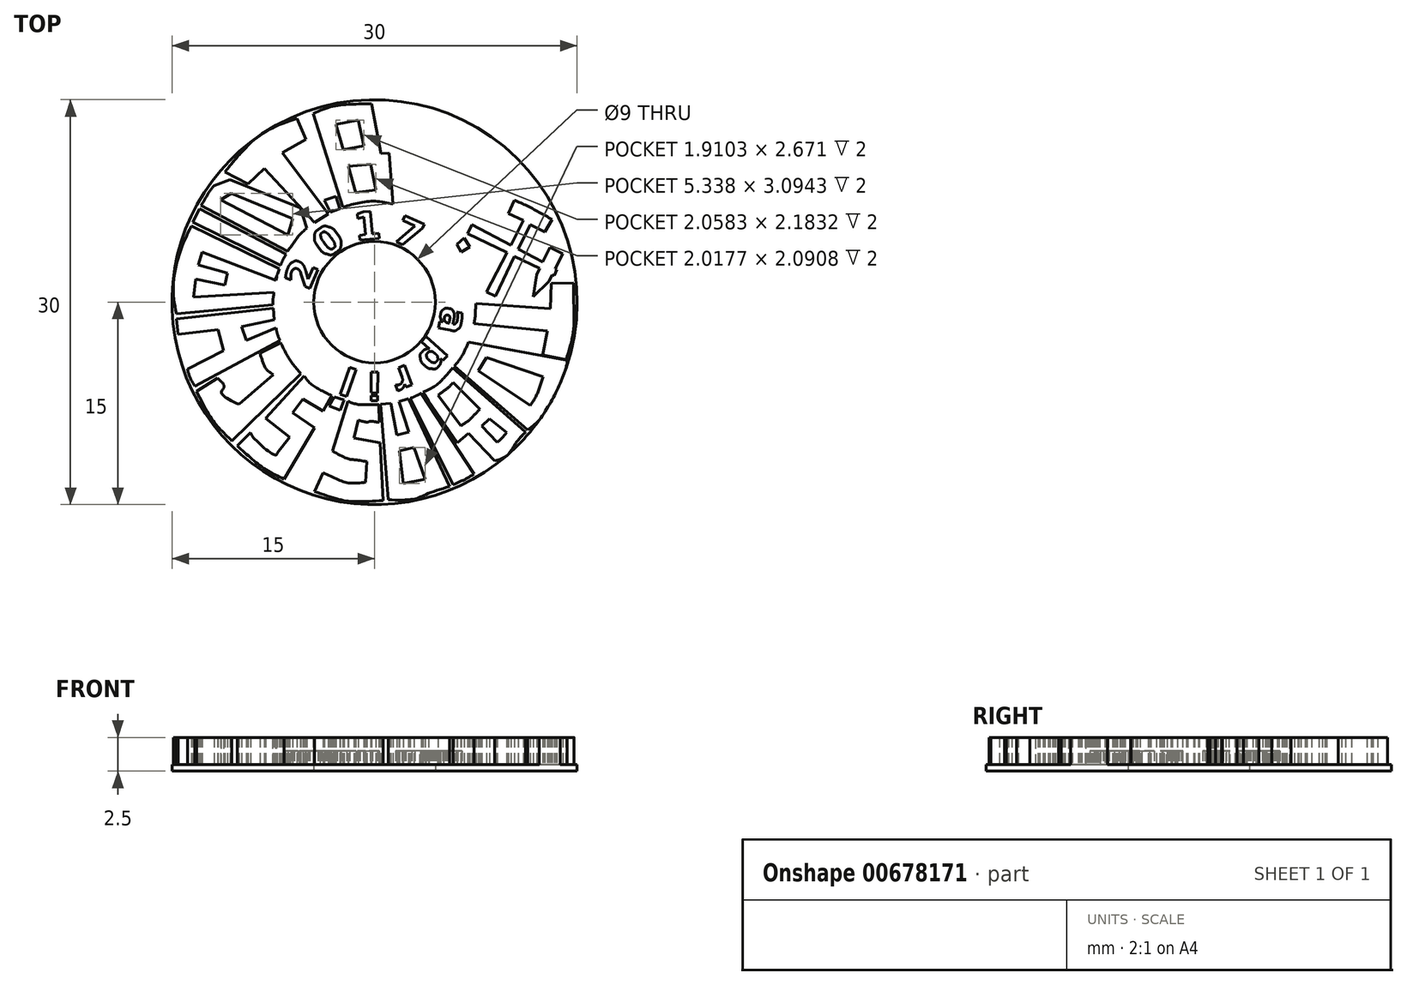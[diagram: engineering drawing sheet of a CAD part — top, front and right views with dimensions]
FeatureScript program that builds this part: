
annotation { "Feature Type Name" : "Feature", "Feature Type Description" : "" }
export const myFeature = defineFeature(function(context is Context, id is Id, definition is map)
    precondition{}
    {
        {
            var Q0;
            Q0=qCreatedBy(makeId("Top.planeOp"),FACE);
            var sketch = newSketch(context, id + "F0", { "sketchPlane" : qUnion([Q0])});
            skCircle(sketch, "E0", {"center": v(0, 0) * mm, "radius": 15 * mm});
            skCircle(sketch, "E1", {"center": v(0, 0) * mm, "radius": 4.5 * mm});
            skSolve(sketch);
        }
        {
            var Q0;
            Q0=makeQuery(id+"F0.imprint","IMPRINT",FACE,{"disambiguationData":[TD([[makeQuery(id+"F0.imprint","IMPRINT",EDGE,{"derivedFrom":sQuery(id+"F0.wireOp",EDGE,"E0")}),1.0]])]});
            extrude(context, id + "F1", {"entities" : qUnion([Q0]), "depth" : 0.5 * mm, "offsetDistance" : 25 * mm});
        }
        {
            var Q0;
            Q0=makeQuery(id+"F1.opExtrude","CAP_FACE",FACE,{"disambiguationData":[OSD([sQuery(id+"F0.wireOp",EDGE,"E0"),sQuery(id+"F0.wireOp",EDGE,"E1")])],"isStart":false});
            var sketch = newSketch(context, id + "F2", { "sketchPlane" : qUnion([Q0])});
            skFitSpline(sketch, "E2", {"points": [v(14.73, 1.43) * mm, v(14.75, -0.4) * mm, v(14.7, -2.22) * mm, v(14.19, -4.26) * mm]});
            skFitSpline(sketch, "E3", {"points": [v(7.35, -1.6) * mm, v(7.45, -1.1) * mm, v(7.47, -0.6) * mm, v(7.51, -0.08) * mm]});
            skLineSegment(sketch, "E4", {"start": v(14.19, -4.26) * mm, "end": v(12.44, -3.92) * mm});
            skLineSegment(sketch, "E5", {"start": v(12.44, -3.92) * mm, "end": v(12.8, -2.13) * mm});
            skLineSegment(sketch, "E6", {"start": v(12.8, -2.13) * mm, "end": v(7.35, -1.6) * mm});
            skLineSegment(sketch, "E7", {"start": v(7.51, -0.08) * mm, "end": v(13.02, -0.47) * mm});
            skLineSegment(sketch, "E8", {"start": v(13.02, -0.47) * mm, "end": v(13.07, 1.4) * mm});
            skLineSegment(sketch, "E9", {"start": v(13.07, 1.4) * mm, "end": v(14.73, 1.43) * mm});
            skFitSpline(sketch, "E10", {"points": [v(11.53, -7.64) * mm, v(11.97, -6.94) * mm, v(12.25, -6.24) * mm, v(12.47, -5.53) * mm]});
            skLineSegment(sketch, "E11", {"start": v(12.47, -5.53) * mm, "end": v(8.28, -4.1) * mm});
            skLineSegment(sketch, "E12", {"start": v(8.28, -4.1) * mm, "end": v(7.7, -5.08) * mm});
            skLineSegment(sketch, "E13", {"start": v(7.7, -5.08) * mm, "end": v(11.53, -7.64) * mm});
            skLineSegment(sketch, "E14", {"start": v(11.53, -7.64) * mm, "end": v(12.47, -5.53) * mm});
            skFitSpline(sketch, "E15", {"points": [v(5.91, -4.73) * mm, v(6.38, -4.14) * mm, v(6.7, -3.55) * mm, v(6.95, -2.96) * mm]});
            skLineSegment(sketch, "E16", {"start": v(11.34, -9.46) * mm, "end": v(5.91, -4.73) * mm});
            skLineSegment(sketch, "E17", {"start": v(5.91, -4.73) * mm, "end": v(11.34, -9.46) * mm});
            skFitSpline(sketch, "E18", {"points": [v(14.15, -4.3) * mm, v(14.25, -4.34) * mm, v(12.79, -7.94) * mm, v(11.34, -9.46) * mm]});
            skLineSegment(sketch, "E19", {"start": v(6.95, -2.96) * mm, "end": v(14.15, -4.3) * mm});
            skLineSegment(sketch, "E20", {"start": v(14.15, -4.3) * mm, "end": v(6.95, -2.96) * mm});
            skFitSpline(sketch, "E21", {"points": [v(9.07, -10.38) * mm, v(9.34, -10.18) * mm, v(9.55, -9.92) * mm, v(9.77, -9.67) * mm]});
            skLineSegment(sketch, "E22", {"start": v(7.95, -9.18) * mm, "end": v(9.07, -10.38) * mm});
            skLineSegment(sketch, "E23", {"start": v(9.07, -10.38) * mm, "end": v(7.95, -9.18) * mm});
            skLineSegment(sketch, "E24", {"start": v(9.77, -9.67) * mm, "end": v(8.52, -8.63) * mm});
            skLineSegment(sketch, "E25", {"start": v(8.52, -8.63) * mm, "end": v(7.95, -9.18) * mm});
            skFitSpline(sketch, "E26", {"points": [v(6.39, -9.15) * mm, v(6.92, -8.8) * mm, v(7.37, -8.37) * mm, v(7.8, -7.93) * mm]});
            skLineSegment(sketch, "E27", {"start": v(4.7, -6.9) * mm, "end": v(6.39, -9.15) * mm});
            skLineSegment(sketch, "E28", {"start": v(6.39, -9.15) * mm, "end": v(4.7, -6.9) * mm});
            skFitSpline(sketch, "E29", {"points": [v(5.82, -5.94) * mm, v(5.5, -6.3) * mm, v(5.1, -6.6) * mm, v(4.7, -6.9) * mm]});
            skLineSegment(sketch, "E30", {"start": v(7.8, -7.93) * mm, "end": v(5.82, -5.94) * mm});
            skLineSegment(sketch, "E31", {"start": v(5.82, -5.94) * mm, "end": v(7.8, -7.93) * mm});
            skFitSpline(sketch, "E32", {"points": [v(3.58, -6.68) * mm, v(4.51, -6.2) * mm, v(5.17, -5.57) * mm, v(5.8, -4.86) * mm]});
            skLineSegment(sketch, "E33", {"start": v(4, -7.35) * mm, "end": v(3.58, -6.68) * mm});
            skLineSegment(sketch, "E34", {"start": v(3.58, -6.68) * mm, "end": v(4, -7.35) * mm});
            skFitSpline(sketch, "E35", {"points": [v(11.17, -9.64) * mm, v(10.5, -10.38) * mm, v(9.8, -11.35) * mm, v(8.9, -11.76) * mm]});
            skLineSegment(sketch, "E36", {"start": v(5.8, -4.86) * mm, "end": v(11.17, -9.64) * mm});
            skLineSegment(sketch, "E37", {"start": v(11.17, -9.64) * mm, "end": v(5.8, -4.86) * mm});
            skFitSpline(sketch, "E38", {"points": [v(7.35, -12.74) * mm, v(6.84, -13.06) * mm, v(6.33, -13.3) * mm, v(5.82, -13.51) * mm]});
            skLineSegment(sketch, "E39", {"start": v(6.96, -9.71) * mm, "end": v(6.12, -10.4) * mm});
            skLineSegment(sketch, "E40", {"start": v(6.12, -10.4) * mm, "end": v(6.96, -9.71) * mm});
            skFitSpline(sketch, "E41", {"points": [v(2.65, -7.13) * mm, v(2.9, -7.02) * mm, v(3.15, -6.9) * mm, v(3.45, -6.75) * mm]});
            skLineSegment(sketch, "E42", {"start": v(5.82, -13.51) * mm, "end": v(2.65, -7.13) * mm});
            skLineSegment(sketch, "E43", {"start": v(2.65, -7.13) * mm, "end": v(5.82, -13.51) * mm});
            skLineSegment(sketch, "E44", {"start": v(3.45, -6.75) * mm, "end": v(7.35, -12.74) * mm});
            skLineSegment(sketch, "E45", {"start": v(7.35, -12.74) * mm, "end": v(3.45, -6.75) * mm});
            skFitSpline(sketch, "E46", {"points": [v(5.56, -13.64) * mm, v(3.67, -14.3) * mm, v(2.99, -14.58) * mm, v(1.01, -14.65) * mm]});
            skLineSegment(sketch, "E47", {"start": v(1.66, -9.85) * mm, "end": v(2.55, -9.63) * mm});
            skLineSegment(sketch, "E48", {"start": v(2.55, -9.63) * mm, "end": v(1.8, -7.38) * mm});
            skLineSegment(sketch, "E49", {"start": v(1.8, -7.38) * mm, "end": v(2.5, -7.14) * mm});
            skLineSegment(sketch, "E50", {"start": v(2.5, -7.14) * mm, "end": v(5.56, -13.64) * mm});
            skLineSegment(sketch, "E51", {"start": v(1.01, -14.65) * mm, "end": v(0.45, -7.57) * mm});
            skLineSegment(sketch, "E52", {"start": v(0.45, -7.57) * mm, "end": v(1.21, -7.5) * mm});
            skLineSegment(sketch, "E53", {"start": v(1.21, -7.5) * mm, "end": v(1.66, -9.85) * mm});
            skLineSegment(sketch, "E54", {"start": v(1.84, -11.03) * mm, "end": v(2.12, -13.45) * mm});
            skLineSegment(sketch, "E55", {"start": v(2.12, -13.45) * mm, "end": v(1.84, -11.03) * mm});
            skFitSpline(sketch, "E56", {"points": [v(-3.82, -12.64) * mm, v(-2.69, -13.16) * mm, v(-1.78, -13.4) * mm, v(-0.65, -13.34) * mm]});
            skLineSegment(sketch, "E57", {"start": v(3.75, -13.1) * mm, "end": v(2.9, -10.78) * mm});
            skLineSegment(sketch, "E58", {"start": v(2.9, -10.78) * mm, "end": v(1.84, -11.03) * mm});
            skFitSpline(sketch, "E59", {"points": [v(-0.58, -11.82) * mm, v(-1.52, -11.67) * mm, v(-1.91, -11.62) * mm, v(-3.13, -11.03) * mm]});
            skLineSegment(sketch, "E60", {"start": v(-0.65, -13.34) * mm, "end": v(-0.58, -11.82) * mm});
            skLineSegment(sketch, "E61", {"start": v(-0.58, -11.82) * mm, "end": v(-0.65, -13.34) * mm});
            skFitSpline(sketch, "E62", {"points": [v(-1.96, -7.34) * mm, v(-1.27, -7.57) * mm, v(-0.48, -7.6) * mm, v(0.31, -7.6) * mm]});
            skLineSegment(sketch, "E63", {"start": v(-3.13, -11.03) * mm, "end": v(-1.96, -7.34) * mm});
            skLineSegment(sketch, "E64", {"start": v(-1.96, -7.34) * mm, "end": v(-3.13, -11.03) * mm});
            skFitSpline(sketch, "E65", {"points": [v(0.36, -8.9) * mm, v(-0.37, -8.84) * mm, v(-0.5, -8.88) * mm, v(-1.2, -8.75) * mm]});
            skLineSegment(sketch, "E66", {"start": v(0.31, -7.6) * mm, "end": v(0.36, -8.9) * mm});
            skLineSegment(sketch, "E67", {"start": v(0.36, -8.9) * mm, "end": v(0.31, -7.6) * mm});
            skFitSpline(sketch, "E68", {"points": [v(0.63, -14.69) * mm, v(-1.45, -14.77) * mm, v(-2.66, -14.61) * mm, v(-4.45, -14.02) * mm]});
            skLineSegment(sketch, "E69", {"start": v(-1.2, -8.75) * mm, "end": v(-1.54, -10.08) * mm});
            skLineSegment(sketch, "E70", {"start": v(-1.54, -10.08) * mm, "end": v(0.43, -10.4) * mm});
            skLineSegment(sketch, "E71", {"start": v(0.43, -10.4) * mm, "end": v(0.63, -14.69) * mm});
            skLineSegment(sketch, "E72", {"start": v(-4.45, -14.02) * mm, "end": v(-3.82, -12.64) * mm});
            skLineSegment(sketch, "E73", {"start": v(-3.82, -12.64) * mm, "end": v(-4.45, -14.02) * mm});
            skFitSpline(sketch, "E74", {"points": [v(-9.19, -9.65) * mm, v(-8.9, -10.1) * mm, v(-7.32, -11.34) * mm, v(-7.2, -11.17) * mm]});
            skLineSegment(sketch, "E75", {"start": v(-2.54, -8) * mm, "end": v(-3.35, -7.68) * mm});
            skLineSegment(sketch, "E76", {"start": v(-3.35, -7.68) * mm, "end": v(-2.98, -7.03) * mm});
            skLineSegment(sketch, "E77", {"start": v(-2.98, -7.03) * mm, "end": v(-2.27, -7.26) * mm});
            skLineSegment(sketch, "E78", {"start": v(-2.27, -7.26) * mm, "end": v(-2.54, -8) * mm});
            skFitSpline(sketch, "E79", {"points": [v(-5.21, -5.46) * mm, v(-4.86, -5.92) * mm, v(-4.15, -6.42) * mm, v(-3.16, -6.93) * mm]});
            skLineSegment(sketch, "E80", {"start": v(-7.2, -11.17) * mm, "end": v(-6.28, -9.99) * mm});
            skLineSegment(sketch, "E81", {"start": v(-6.28, -9.99) * mm, "end": v(-7.2, -11.17) * mm});
            skFitSpline(sketch, "E82", {"points": [v(-6.7, -13.1) * mm, v(-8, -12.43) * mm, v(-9.12, -11.58) * mm, v(-10.16, -10.64) * mm]});
            skLineSegment(sketch, "E83", {"start": v(-3.16, -6.93) * mm, "end": v(-3.8, -8.06) * mm});
            skLineSegment(sketch, "E84", {"start": v(-3.8, -8.06) * mm, "end": v(-5.29, -7.16) * mm});
            skLineSegment(sketch, "E85", {"start": v(-5.29, -7.16) * mm, "end": v(-6.05, -8.18) * mm});
            skLineSegment(sketch, "E86", {"start": v(-6.05, -8.18) * mm, "end": v(-4.45, -9.3) * mm});
            skLineSegment(sketch, "E87", {"start": v(-4.45, -9.3) * mm, "end": v(-6.7, -13.1) * mm});
            skFitSpline(sketch, "E88", {"points": [v(-6.95, -3) * mm, v(-6.51, -3.87) * mm, v(-6.05, -4.59) * mm, v(-5.45, -5.3) * mm]});
            skLineSegment(sketch, "E89", {"start": v(-10.16, -10.64) * mm, "end": v(-9.19, -9.65) * mm});
            skLineSegment(sketch, "E90", {"start": v(-9.19, -9.65) * mm, "end": v(-10.16, -10.64) * mm});
            skFitSpline(sketch, "E91", {"points": [v(-10.56, -10.28) * mm, v(-11.34, -9.5) * mm, v(-12.13, -8.55) * mm, v(-13.18, -6.6) * mm]});
            skLineSegment(sketch, "E92", {"start": v(-5.45, -5.3) * mm, "end": v(-10.56, -10.28) * mm});
            skLineSegment(sketch, "E93", {"start": v(-10.56, -10.28) * mm, "end": v(-5.45, -5.3) * mm});
            skFitSpline(sketch, "E94", {"points": [v(-11.62, -5.63) * mm, v(-11.14, -6.26) * mm, v(-11.33, -6.7) * mm, v(-10.05, -7.57) * mm]});
            skLineSegment(sketch, "E95", {"start": v(-13.18, -6.6) * mm, "end": v(-11.62, -5.63) * mm});
            skLineSegment(sketch, "E96", {"start": v(-11.62, -5.63) * mm, "end": v(-13.18, -6.6) * mm});
            skFitSpline(sketch, "E97", {"points": [v(-7.49, -5.38) * mm, v(-8.05, -4.92) * mm, v(-8.3, -4.36) * mm, v(-8.48, -3.8) * mm]});
            skLineSegment(sketch, "E98", {"start": v(-10.05, -7.57) * mm, "end": v(-7.49, -5.38) * mm});
            skLineSegment(sketch, "E99", {"start": v(-7.49, -5.38) * mm, "end": v(-10.05, -7.57) * mm});
            skFitSpline(sketch, "E100", {"points": [v(-13.32, -6.22) * mm, v(-13.55, -5.82) * mm, v(-13.73, -5.4) * mm, v(-13.85, -4.96) * mm]});
            skLineSegment(sketch, "E101", {"start": v(-8.48, -3.8) * mm, "end": v(-6.95, -3) * mm});
            skLineSegment(sketch, "E102", {"start": v(-6.95, -3) * mm, "end": v(-8.48, -3.8) * mm});
            skFitSpline(sketch, "E103", {"points": [v(-7.3, -1.92) * mm, v(-7.22, -2.26) * mm, v(-7.12, -2.56) * mm, v(-7, -2.84) * mm]});
            skLineSegment(sketch, "E104", {"start": v(-13.85, -4.96) * mm, "end": v(-11.17, -3.6) * mm});
            skLineSegment(sketch, "E105", {"start": v(-11.17, -3.6) * mm, "end": v(-11.6, -2.05) * mm});
            skLineSegment(sketch, "E106", {"start": v(-11.6, -2.05) * mm, "end": v(-14.54, -2.4) * mm});
            skLineSegment(sketch, "E107", {"start": v(-14.54, -2.4) * mm, "end": v(-14.67, -1.23) * mm});
            skLineSegment(sketch, "E108", {"start": v(-14.67, -1.23) * mm, "end": v(-7.5, -0.45) * mm});
            skLineSegment(sketch, "E109", {"start": v(-7.5, -0.45) * mm, "end": v(-7.42, -1.31) * mm});
            skLineSegment(sketch, "E110", {"start": v(-7.42, -1.31) * mm, "end": v(-9.83, -1.81) * mm});
            skLineSegment(sketch, "E111", {"start": v(-9.83, -1.81) * mm, "end": v(-9.5, -2.83) * mm});
            skLineSegment(sketch, "E112", {"start": v(-9.5, -2.83) * mm, "end": v(-7.3, -1.92) * mm});
            skFitSpline(sketch, "E113", {"points": [v(-14.68, -0.86) * mm, v(-14.9, 1.2) * mm, v(-14.4, 3.7) * mm, v(-13.56, 5.66) * mm]});
            skLineSegment(sketch, "E114", {"start": v(-7, -2.84) * mm, "end": v(-13.32, -6.22) * mm});
            skLineSegment(sketch, "E115", {"start": v(-13.32, -6.22) * mm, "end": v(-7, -2.84) * mm});
            skFitSpline(sketch, "E116", {"points": [v(-7.04, 2.48) * mm, v(-7.3, 1.75) * mm, v(-7.24, 1.88) * mm, v(-7.3, 1.6) * mm]});
            skLineSegment(sketch, "E117", {"start": v(-13.56, 5.66) * mm, "end": v(-7.04, 2.48) * mm});
            skLineSegment(sketch, "E118", {"start": v(-7.04, 2.48) * mm, "end": v(-13.56, 5.66) * mm});
            skFitSpline(sketch, "E119", {"points": [v(-7.45, 0.73) * mm, v(-7.5, 0.36) * mm, v(-7.53, 0.17) * mm, v(-7.52, -0.2) * mm]});
            skLineSegment(sketch, "E120", {"start": v(-7.3, 1.6) * mm, "end": v(-12.78, 3.7) * mm});
            skLineSegment(sketch, "E121", {"start": v(-12.78, 3.7) * mm, "end": v(-13.06, 2.74) * mm});
            skLineSegment(sketch, "E122", {"start": v(-13.06, 2.74) * mm, "end": v(-10.9, 2.16) * mm});
            skLineSegment(sketch, "E123", {"start": v(-10.9, 2.16) * mm, "end": v(-11.08, 1.28) * mm});
            skLineSegment(sketch, "E124", {"start": v(-11.08, 1.28) * mm, "end": v(-13.25, 1.7) * mm});
            skLineSegment(sketch, "E125", {"start": v(-13.25, 1.7) * mm, "end": v(-13.4, 0.36) * mm});
            skLineSegment(sketch, "E126", {"start": v(-13.4, 0.36) * mm, "end": v(-7.45, 0.73) * mm});
            skLineSegment(sketch, "E127", {"start": v(-7.52, -0.2) * mm, "end": v(-14.68, -0.86) * mm});
            skLineSegment(sketch, "E128", {"start": v(-14.68, -0.86) * mm, "end": v(-7.52, -0.2) * mm});
            skFitSpline(sketch, "E129", {"points": [v(-6.55, 3.54) * mm, v(-6.71, 3.27) * mm, v(-6.85, 3) * mm, v(-6.96, 2.73) * mm]});
            skLineSegment(sketch, "E130", {"start": v(-13.47, 5.94) * mm, "end": v(-12.97, 6.91) * mm});
            skLineSegment(sketch, "E131", {"start": v(-12.97, 6.91) * mm, "end": v(-6.55, 3.54) * mm});
            skLineSegment(sketch, "E132", {"start": v(-6.96, 2.73) * mm, "end": v(-13.47, 5.94) * mm});
            skLineSegment(sketch, "E133", {"start": v(-13.47, 5.94) * mm, "end": v(-6.96, 2.73) * mm});
            skLineSegment(sketch, "E134", {"start": v(-11.41, 7.57) * mm, "end": v(-6.42, 4.98) * mm});
            skLineSegment(sketch, "E135", {"start": v(-6.42, 4.98) * mm, "end": v(-6.07, 6.2) * mm});
            skLineSegment(sketch, "E136", {"start": v(-6.07, 6.2) * mm, "end": v(-10.6, 8.08) * mm});
            skLineSegment(sketch, "E137", {"start": v(-10.6, 8.08) * mm, "end": v(-11.41, 7.57) * mm});
            skFitSpline(sketch, "E138", {"points": [v(-5, 5.48) * mm, v(-5.61, 4.92) * mm, v(-6.05, 4.3) * mm, v(-6.45, 3.78) * mm]});
            skLineSegment(sketch, "E139", {"start": v(-11.88, 8.63) * mm, "end": v(-10.7, 9.08) * mm});
            skLineSegment(sketch, "E140", {"start": v(-10.7, 9.08) * mm, "end": v(-5.49, 6.98) * mm});
            skLineSegment(sketch, "E141", {"start": v(-5.49, 6.98) * mm, "end": v(-5, 5.48) * mm});
            skFitSpline(sketch, "E142", {"points": [v(-12.85, 7.16) * mm, v(-12.55, 7.64) * mm, v(-12.28, 8.1) * mm, v(-11.88, 8.63) * mm]});
            skLineSegment(sketch, "E143", {"start": v(-6.45, 3.78) * mm, "end": v(-12.85, 7.16) * mm});
            skLineSegment(sketch, "E144", {"start": v(-12.85, 7.16) * mm, "end": v(-6.45, 3.78) * mm});
            skFitSpline(sketch, "E145", {"points": [v(-11.09, 9.64) * mm, v(-9.23, 11.74) * mm, v(-7.65, 12.86) * mm, v(-5.74, 13.62) * mm]});
            skLineSegment(sketch, "E146", {"start": v(-5.74, 13.62) * mm, "end": v(-5.1, 12.06) * mm});
            skLineSegment(sketch, "E147", {"start": v(-5.1, 12.06) * mm, "end": v(-6.83, 11.07) * mm});
            skLineSegment(sketch, "E148", {"start": v(-6.83, 11.07) * mm, "end": v(-3.44, 6.55) * mm});
            skLineSegment(sketch, "E149", {"start": v(-3.44, 6.55) * mm, "end": v(-4.46, 5.9) * mm});
            skLineSegment(sketch, "E150", {"start": v(-4.46, 5.9) * mm, "end": v(-8.17, 9.89) * mm});
            skLineSegment(sketch, "E151", {"start": v(-8.17, 9.89) * mm, "end": v(-9.35, 8.76) * mm});
            skLineSegment(sketch, "E152", {"start": v(-9.35, 8.76) * mm, "end": v(-11.09, 9.64) * mm});
            skLineSegment(sketch, "E153", {"start": v(-3.71, 7.54) * mm, "end": v(-2.87, 7.83) * mm});
            skLineSegment(sketch, "E154", {"start": v(-2.87, 7.83) * mm, "end": v(-2.58, 6.92) * mm});
            skLineSegment(sketch, "E155", {"start": v(-2.58, 6.92) * mm, "end": v(-3.26, 6.67) * mm});
            skLineSegment(sketch, "E156", {"start": v(-3.26, 6.67) * mm, "end": v(-3.71, 7.54) * mm});
            skLineSegment(sketch, "E157", {"start": v(-1.21, 13.5) * mm, "end": v(-2.84, 13.18) * mm});
            skLineSegment(sketch, "E158", {"start": v(-2.84, 13.18) * mm, "end": v(-2.31, 11.31) * mm});
            skLineSegment(sketch, "E159", {"start": v(-2.31, 11.31) * mm, "end": v(-0.78, 11.6) * mm});
            skLineSegment(sketch, "E160", {"start": v(-0.78, 11.6) * mm, "end": v(-1.21, 13.5) * mm});
            skFitSpline(sketch, "E161", {"points": [v(1.37, 7.27) * mm, v(0.13, 7.47) * mm, v(-1.11, 7.37) * mm, v(-2.35, 7.04) * mm]});
            skLineSegment(sketch, "E162", {"start": v(0.1, 8.3) * mm, "end": v(-0.28, 10.22) * mm});
            skLineSegment(sketch, "E163", {"start": v(-0.28, 10.22) * mm, "end": v(-1.93, 10.06) * mm});
            skLineSegment(sketch, "E164", {"start": v(-1.93, 10.06) * mm, "end": v(-1.4, 8.13) * mm});
            skLineSegment(sketch, "E165", {"start": v(-1.4, 8.13) * mm, "end": v(0.1, 8.3) * mm});
            skFitSpline(sketch, "E166", {"points": [v(-4.54, 13.98) * mm, v(-3.1, 14.5) * mm, v(-1.66, 14.66) * mm, v(-0.22, 14.71) * mm]});
            skLineSegment(sketch, "E167", {"start": v(-2.35, 7.04) * mm, "end": v(-4.54, 13.98) * mm});
            skLineSegment(sketch, "E168", {"start": v(-4.54, 13.98) * mm, "end": v(-2.35, 7.04) * mm});
            skLineSegment(sketch, "E169", {"start": v(-0.22, 14.71) * mm, "end": v(0.5, 11.02) * mm});
            skLineSegment(sketch, "E170", {"start": v(0.5, 11.02) * mm, "end": v(-0.22, 14.71) * mm});
            skLineSegment(sketch, "E171", {"start": v(1.08, 11.05) * mm, "end": v(1.37, 7.27) * mm});
            skLineSegment(sketch, "E172", {"start": v(1.37, 7.27) * mm, "end": v(1.08, 11.05) * mm});
            skLineSegment(sketch, "E173", {"start": v(5.12, 12.03) * mm, "end": v(2.66, 12.72) * mm});
            skLineSegment(sketch, "E174", {"start": v(2.66, 12.72) * mm, "end": v(5.12, 12.03) * mm});
            skFitSpline(sketch, "E175", {"points": [v(4.36, 6) * mm, v(3.46, 6.62) * mm, v(1.52, 7.3) * mm, v(1.5, 7.23) * mm]});
            skLineSegment(sketch, "E176", {"start": v(2.62, 11.45) * mm, "end": v(4.8, 10.63) * mm});
            skLineSegment(sketch, "E177", {"start": v(4.8, 10.63) * mm, "end": v(4.36, 6) * mm});
            skFitSpline(sketch, "E178", {"points": [v(1.3, 14.64) * mm, v(2.74, 14.5) * mm, v(4.13, 14.23) * mm, v(5.35, 13.67) * mm]});
            skLineSegment(sketch, "E179", {"start": v(1.5, 7.23) * mm, "end": v(1.55, 8.78) * mm});
            skLineSegment(sketch, "E180", {"start": v(1.55, 8.78) * mm, "end": v(3.73, 7.9) * mm});
            skLineSegment(sketch, "E181", {"start": v(3.73, 7.9) * mm, "end": v(3.8, 9.25) * mm});
            skLineSegment(sketch, "E182", {"start": v(3.8, 9.25) * mm, "end": v(1.5, 10.2) * mm});
            skLineSegment(sketch, "E183", {"start": v(1.5, 10.2) * mm, "end": v(1.3, 14.64) * mm});
            skLineSegment(sketch, "E184", {"start": v(5.35, 13.67) * mm, "end": v(5.12, 12.03) * mm});
            skLineSegment(sketch, "E185", {"start": v(5.12, 12.03) * mm, "end": v(5.35, 13.67) * mm});
            skLineSegment(sketch, "E186", {"start": v(8.2, 8.17) * mm, "end": v(7.57, 6.97) * mm});
            skLineSegment(sketch, "E187", {"start": v(7.57, 6.97) * mm, "end": v(8.2, 8.17) * mm});
            skFitSpline(sketch, "E188", {"points": [v(5.97, 4.44) * mm, v(5.57, 4.9) * mm, v(5.23, 5.26) * mm, v(4.56, 5.82) * mm]});
            skLineSegment(sketch, "E189", {"start": v(6.2, 8.12) * mm, "end": v(5.73, 6.4) * mm});
            skLineSegment(sketch, "E190", {"start": v(5.73, 6.4) * mm, "end": v(6.73, 5.34) * mm});
            skLineSegment(sketch, "E191", {"start": v(6.73, 5.34) * mm, "end": v(5.97, 4.44) * mm});
            skLineSegment(sketch, "E192", {"start": v(4.56, 5.82) * mm, "end": v(5.43, 10.26) * mm});
            skLineSegment(sketch, "E193", {"start": v(5.43, 10.26) * mm, "end": v(8.2, 8.17) * mm});
            skLineSegment(sketch, "E194", {"start": v(6.63, 4.74) * mm, "end": v(7.05, 4.1) * mm});
            skLineSegment(sketch, "E195", {"start": v(7.05, 4.1) * mm, "end": v(6.42, 3.72) * mm});
            skLineSegment(sketch, "E196", {"start": v(6.42, 3.72) * mm, "end": v(6.09, 4.28) * mm});
            skLineSegment(sketch, "E197", {"start": v(6.09, 4.28) * mm, "end": v(6.63, 4.74) * mm});
            skFitSpline(sketch, "E198", {"points": [v(10.34, 7.56) * mm, v(11.24, 7.16) * mm, v(12.2, 6.65) * mm, v(13.15, 6.13) * mm]});
            skLineSegment(sketch, "E199", {"start": v(13.15, 2.04) * mm, "end": v(12.92, 1.57) * mm});
            skLineSegment(sketch, "E200", {"start": v(12.92, 1.57) * mm, "end": v(11.75, 0.4) * mm});
            skLineSegment(sketch, "E201", {"start": v(11.75, 0.4) * mm, "end": v(11.99, 2.04) * mm});
            skLineSegment(sketch, "E202", {"start": v(11.99, 2.04) * mm, "end": v(12.22, 2.5) * mm});
            skLineSegment(sketch, "E203", {"start": v(12.22, 2.5) * mm, "end": v(10.36, 3.4) * mm});
            skLineSegment(sketch, "E204", {"start": v(10.36, 3.4) * mm, "end": v(8.94, 0.43) * mm});
            skLineSegment(sketch, "E205", {"start": v(8.94, 0.43) * mm, "end": v(8.28, 0.77) * mm});
            skLineSegment(sketch, "E206", {"start": v(8.28, 0.77) * mm, "end": v(9.8, 3.67) * mm});
            skLineSegment(sketch, "E207", {"start": v(9.8, 3.67) * mm, "end": v(6.89, 5.09) * mm});
            skLineSegment(sketch, "E208", {"start": v(6.89, 5.09) * mm, "end": v(7.22, 5.76) * mm});
            skLineSegment(sketch, "E209", {"start": v(7.22, 5.76) * mm, "end": v(10.1, 4.23) * mm});
            skLineSegment(sketch, "E210", {"start": v(10.1, 4.23) * mm, "end": v(11.02, 6.06) * mm});
            skLineSegment(sketch, "E211", {"start": v(11.02, 6.06) * mm, "end": v(9.92, 6.56) * mm});
            skLineSegment(sketch, "E212", {"start": v(9.92, 6.56) * mm, "end": v(10.34, 7.56) * mm});
            skFitSpline(sketch, "E213", {"points": [v(5.56, -1.3) * mm, v(5.58, -1.2) * mm, v(5.58, -1.12) * mm, v(5.55, -1.06) * mm]});
            skFitSpline(sketch, "E214", {"points": [v(5.55, -1.06) * mm, v(5.53, -1) * mm, v(5.48, -0.97) * mm, v(5.42, -0.96) * mm]});
            skFitSpline(sketch, "E215", {"points": [v(5.42, -0.96) * mm, v(5.35, -0.95) * mm, v(5.3, -0.96) * mm, v(5.26, -1) * mm]});
            skFitSpline(sketch, "E216", {"points": [v(5.26, -1) * mm, v(5.22, -1.03) * mm, v(5.19, -1.08) * mm, v(5.17, -1.15) * mm]});
            skFitSpline(sketch, "E217", {"points": [v(5.17, -1.15) * mm, v(5.16, -1.24) * mm, v(5.17, -1.33) * mm, v(5.23, -1.4) * mm]});
            skFitSpline(sketch, "E218", {"points": [v(5.23, -1.4) * mm, v(5.28, -1.48) * mm, v(5.36, -1.52) * mm, v(5.45, -1.54) * mm]});
            skLineSegment(sketch, "E219", {"start": v(13.15, 6.13) * mm, "end": v(12.6, 5.2) * mm});
            skLineSegment(sketch, "E220", {"start": v(12.6, 5.2) * mm, "end": v(11.53, 5.75) * mm});
            skLineSegment(sketch, "E221", {"start": v(11.53, 5.75) * mm, "end": v(10.63, 3.94) * mm});
            skLineSegment(sketch, "E222", {"start": v(10.63, 3.94) * mm, "end": v(12.46, 2.97) * mm});
            skLineSegment(sketch, "E223", {"start": v(12.46, 2.97) * mm, "end": v(13, 4.05) * mm});
            skLineSegment(sketch, "E224", {"start": v(13, 4.05) * mm, "end": v(13.92, 3.58) * mm});
            skLineSegment(sketch, "E225", {"start": v(13.92, 3.58) * mm, "end": v(13.38, 2.48) * mm});
            skLineSegment(sketch, "E226", {"start": v(13.38, 2.48) * mm, "end": v(13.5, 2.41) * mm});
            skLineSegment(sketch, "E227", {"start": v(13.5, 2.41) * mm, "end": v(13.29, 1.98) * mm});
            skLineSegment(sketch, "E228", {"start": v(13.29, 1.98) * mm, "end": v(13.15, 2.04) * mm});
            skLineSegment(sketch, "E229", {"start": v(5.45, -1.54) * mm, "end": v(5.51, -1.55) * mm});
            skLineSegment(sketch, "E230", {"start": v(5.51, -1.55) * mm, "end": v(5.56, -1.3) * mm});
            skLineSegment(sketch, "E231", {"start": v(5.56, -1.3) * mm, "end": v(5.56, -1.3) * mm});
            skFitSpline(sketch, "E232", {"points": [v(5.05, -1.47) * mm, v(4.97, -1.38) * mm, v(4.92, -1.3) * mm, v(4.9, -1.2) * mm]});
            skFitSpline(sketch, "E233", {"points": [v(4.9, -1.2) * mm, v(4.87, -1.12) * mm, v(4.87, -1.02) * mm, v(4.89, -0.9) * mm]});
            skFitSpline(sketch, "E234", {"points": [v(4.89, -0.9) * mm, v(4.92, -0.74) * mm, v(5, -0.62) * mm, v(5.1, -0.54) * mm]});
            skFitSpline(sketch, "E235", {"points": [v(5.1, -0.54) * mm, v(5.21, -0.46) * mm, v(5.34, -0.44) * mm, v(5.49, -0.47) * mm]});
            skFitSpline(sketch, "E236", {"points": [v(5.49, -0.47) * mm, v(5.66, -0.5) * mm, v(5.78, -0.59) * mm, v(5.84, -0.73) * mm]});
            skFitSpline(sketch, "E237", {"points": [v(5.84, -0.73) * mm, v(5.9, -0.86) * mm, v(5.9, -1.06) * mm, v(5.85, -1.33) * mm]});
            skLineSegment(sketch, "E238", {"start": v(5.6, -2.08) * mm, "end": v(4.73, -1.91) * mm});
            skLineSegment(sketch, "E239", {"start": v(4.73, -1.91) * mm, "end": v(4.83, -1.42) * mm});
            skLineSegment(sketch, "E240", {"start": v(4.83, -1.42) * mm, "end": v(5.05, -1.47) * mm});
            skFitSpline(sketch, "E241", {"points": [v(5.84, -1.62) * mm, v(5.91, -1.63) * mm, v(5.97, -1.61) * mm, v(6.02, -1.56) * mm]});
            skFitSpline(sketch, "E242", {"points": [v(6.02, -1.56) * mm, v(6.07, -1.5) * mm, v(6.1, -1.42) * mm, v(6.13, -1.29) * mm]});
            skFitSpline(sketch, "E243", {"points": [v(6.13, -1.29) * mm, v(6.15, -1.18) * mm, v(6.16, -1.09) * mm, v(6.16, -1) * mm]});
            skFitSpline(sketch, "E244", {"points": [v(6.16, -1) * mm, v(6.15, -0.9) * mm, v(6.14, -0.81) * mm, v(6.11, -0.73) * mm]});
            skLineSegment(sketch, "E245", {"start": v(5.85, -1.33) * mm, "end": v(5.8, -1.61) * mm});
            skLineSegment(sketch, "E246", {"start": v(5.8, -1.61) * mm, "end": v(5.84, -1.62) * mm});
            skFitSpline(sketch, "E247", {"points": [v(6.48, -0.8) * mm, v(6.49, -0.9) * mm, v(6.48, -1.01) * mm, v(6.48, -1.12) * mm]});
            skFitSpline(sketch, "E248", {"points": [v(6.48, -1.12) * mm, v(6.47, -1.23) * mm, v(6.46, -1.33) * mm, v(6.44, -1.44) * mm]});
            skFitSpline(sketch, "E249", {"points": [v(6.44, -1.44) * mm, v(6.38, -1.71) * mm, v(6.29, -1.9) * mm, v(6.16, -2) * mm]});
            skFitSpline(sketch, "E250", {"points": [v(6.16, -2) * mm, v(6.03, -2.1) * mm, v(5.84, -2.13) * mm, v(5.6, -2.08) * mm]});
            skLineSegment(sketch, "E251", {"start": v(6.11, -0.73) * mm, "end": v(6.48, -0.8) * mm});
            skLineSegment(sketch, "E252", {"start": v(6.48, -0.8) * mm, "end": v(6.11, -0.73) * mm});
            skLineSegment(sketch, "E253", {"start": v(5.6, -2.08) * mm, "end": v(5.6, -2.08) * mm});
            skFitSpline(sketch, "E254", {"points": [v(4.9, -4.18) * mm, v(4.92, -4.3) * mm, v(4.92, -4.4) * mm, v(4.9, -4.48) * mm]});
            skFitSpline(sketch, "E255", {"points": [v(4.9, -4.48) * mm, v(4.87, -4.57) * mm, v(4.82, -4.66) * mm, v(4.75, -4.74) * mm]});
            skFitSpline(sketch, "E256", {"points": [v(4.75, -4.74) * mm, v(4.63, -4.88) * mm, v(4.47, -4.95) * mm, v(4.27, -4.94) * mm]});
            skFitSpline(sketch, "E257", {"points": [v(4.27, -4.94) * mm, v(4.08, -4.93) * mm, v(3.9, -4.85) * mm, v(3.71, -4.69) * mm]});
            skFitSpline(sketch, "E258", {"points": [v(3.71, -4.69) * mm, v(3.54, -4.53) * mm, v(3.43, -4.35) * mm, v(3.4, -4.16) * mm]});
            skFitSpline(sketch, "E259", {"points": [v(3.4, -4.16) * mm, v(3.37, -3.97) * mm, v(3.41, -3.8) * mm, v(3.54, -3.66) * mm]});
            skFitSpline(sketch, "E260", {"points": [v(3.54, -3.66) * mm, v(3.61, -3.58) * mm, v(3.7, -3.52) * mm, v(3.78, -3.5) * mm]});
            skFitSpline(sketch, "E261", {"points": [v(3.78, -3.5) * mm, v(3.86, -3.46) * mm, v(3.96, -3.45) * mm, v(4.08, -3.45) * mm]});
            skLineSegment(sketch, "E262", {"start": v(4.08, -3.45) * mm, "end": v(3.47, -2.92) * mm});
            skLineSegment(sketch, "E263", {"start": v(3.47, -2.92) * mm, "end": v(3.8, -2.55) * mm});
            skLineSegment(sketch, "E264", {"start": v(3.8, -2.55) * mm, "end": v(5.4, -3.96) * mm});
            skLineSegment(sketch, "E265", {"start": v(5.4, -3.96) * mm, "end": v(5.06, -4.33) * mm});
            skLineSegment(sketch, "E266", {"start": v(5.06, -4.33) * mm, "end": v(4.9, -4.18) * mm});
            skFitSpline(sketch, "E267", {"points": [v(4.6, -4.36) * mm, v(4.68, -4.28) * mm, v(4.7, -4.2) * mm, v(4.68, -4.1) * mm]});
            skFitSpline(sketch, "E268", {"points": [v(4.68, -4.1) * mm, v(4.66, -4.01) * mm, v(4.6, -3.91) * mm, v(4.49, -3.82) * mm]});
            skFitSpline(sketch, "E269", {"points": [v(4.49, -3.82) * mm, v(4.38, -3.72) * mm, v(4.27, -3.67) * mm, v(4.18, -3.66) * mm]});
            skFitSpline(sketch, "E270", {"points": [v(4.18, -3.66) * mm, v(4.08, -3.65) * mm, v(4, -3.68) * mm, v(3.93, -3.76) * mm]});
            skFitSpline(sketch, "E271", {"points": [v(3.93, -3.76) * mm, v(3.86, -3.84) * mm, v(3.83, -3.93) * mm, v(3.86, -4.02) * mm]});
            skFitSpline(sketch, "E272", {"points": [v(3.86, -4.02) * mm, v(3.88, -4.11) * mm, v(3.94, -4.2) * mm, v(4.05, -4.3) * mm]});
            skFitSpline(sketch, "E273", {"points": [v(4.05, -4.3) * mm, v(4.16, -4.4) * mm, v(4.26, -4.46) * mm, v(4.36, -4.47) * mm]});
            skFitSpline(sketch, "E274", {"points": [v(4.36, -4.47) * mm, v(4.45, -4.48) * mm, v(4.54, -4.44) * mm, v(4.6, -4.36) * mm]});
            skLineSegment(sketch, "E275", {"start": v(4.08, -3.45) * mm, "end": v(4.08, -3.45) * mm});
            skFitSpline(sketch, "E276", {"points": [v(1.56, -6.15) * mm, v(1.6, -6.15) * mm, v(1.65, -6.15) * mm, v(1.7, -6.14) * mm]});
            skFitSpline(sketch, "E277", {"points": [v(1.7, -6.14) * mm, v(1.74, -6.13) * mm, v(1.78, -6.12) * mm, v(1.82, -6.1) * mm]});
            skFitSpline(sketch, "E278", {"points": [v(1.82, -6.1) * mm, v(1.94, -6.06) * mm, v(2.01, -5.99) * mm, v(2.05, -5.89) * mm]});
            skFitSpline(sketch, "E279", {"points": [v(2.05, -5.89) * mm, v(2.08, -5.79) * mm, v(2.07, -5.67) * mm, v(2.02, -5.53) * mm]});
            skFitSpline(sketch, "E280", {"points": [v(2.23, -6.07) * mm, v(2.2, -6.18) * mm, v(2.16, -6.28) * mm, v(2.1, -6.35) * mm]});
            skFitSpline(sketch, "E281", {"points": [v(2.1, -6.35) * mm, v(2.04, -6.42) * mm, v(1.96, -6.48) * mm, v(1.85, -6.52) * mm]});
            skFitSpline(sketch, "E282", {"points": [v(1.85, -6.52) * mm, v(1.83, -6.53) * mm, v(1.82, -6.53) * mm, v(1.8, -6.54) * mm]});
            skFitSpline(sketch, "E283", {"points": [v(1.8, -6.54) * mm, v(1.78, -6.55) * mm, v(1.75, -6.55) * mm, v(1.72, -6.56) * mm]});
            skLineSegment(sketch, "E284", {"start": v(2.02, -5.53) * mm, "end": v(1.76, -4.86) * mm});
            skLineSegment(sketch, "E285", {"start": v(1.76, -4.86) * mm, "end": v(2.23, -4.69) * mm});
            skLineSegment(sketch, "E286", {"start": v(2.23, -4.69) * mm, "end": v(2.78, -6.13) * mm});
            skLineSegment(sketch, "E287", {"start": v(2.78, -6.13) * mm, "end": v(2.32, -6.3) * mm});
            skLineSegment(sketch, "E288", {"start": v(2.32, -6.3) * mm, "end": v(2.23, -6.07) * mm});
            skLineSegment(sketch, "E289", {"start": v(1.72, -6.56) * mm, "end": v(1.56, -6.15) * mm});
            skLineSegment(sketch, "E290", {"start": v(1.56, -6.15) * mm, "end": v(1.56, -6.15) * mm});
            skLineSegment(sketch, "E291", {"start": v(1.56, -6.15) * mm, "end": v(1.72, -6.56) * mm});
            skLineSegment(sketch, "E292", {"start": v(0.23, -6.72) * mm, "end": v(-0.26, -6.72) * mm});
            skLineSegment(sketch, "E293", {"start": v(-0.26, -6.72) * mm, "end": v(-0.25, -5.17) * mm});
            skLineSegment(sketch, "E294", {"start": v(-0.25, -5.17) * mm, "end": v(0.24, -5.18) * mm});
            skLineSegment(sketch, "E295", {"start": v(0.24, -5.18) * mm, "end": v(0.23, -6.72) * mm});
            skLineSegment(sketch, "E296", {"start": v(0.23, -6.72) * mm, "end": v(0.23, -6.72) * mm});
            skLineSegment(sketch, "E297", {"start": v(0.23, -7.32) * mm, "end": v(-0.27, -7.32) * mm});
            skLineSegment(sketch, "E298", {"start": v(-0.27, -7.32) * mm, "end": v(-0.26, -6.91) * mm});
            skLineSegment(sketch, "E299", {"start": v(-0.26, -6.91) * mm, "end": v(0.23, -6.92) * mm});
            skLineSegment(sketch, "E300", {"start": v(0.23, -6.92) * mm, "end": v(0.23, -7.32) * mm});
            skLineSegment(sketch, "E301", {"start": v(0.23, -7.32) * mm, "end": v(0.23, -7.32) * mm});
            skLineSegment(sketch, "E302", {"start": v(-2.08, -7) * mm, "end": v(-2.55, -6.84) * mm});
            skLineSegment(sketch, "E303", {"start": v(-2.55, -6.84) * mm, "end": v(-1.83, -4.81) * mm});
            skLineSegment(sketch, "E304", {"start": v(-1.83, -4.81) * mm, "end": v(-1.37, -4.98) * mm});
            skLineSegment(sketch, "E305", {"start": v(-1.37, -4.98) * mm, "end": v(-2.08, -7) * mm});
            skFitSpline(sketch, "E306", {"points": [v(-5.45, 2.14) * mm, v(-5.48, 2.22) * mm, v(-5.51, 2.3) * mm, v(-5.55, 2.34) * mm]});
            skFitSpline(sketch, "E307", {"points": [v(-5.55, 2.34) * mm, v(-5.6, 2.4) * mm, v(-5.64, 2.44) * mm, v(-5.7, 2.46) * mm]});
            skFitSpline(sketch, "E308", {"points": [v(-5.7, 2.46) * mm, v(-5.79, 2.5) * mm, v(-5.87, 2.5) * mm, v(-5.95, 2.46) * mm]});
            skFitSpline(sketch, "E309", {"points": [v(-5.95, 2.46) * mm, v(-6.03, 2.43) * mm, v(-6.1, 2.36) * mm, v(-6.14, 2.26) * mm]});
            skFitSpline(sketch, "E310", {"points": [v(-6.14, 2.26) * mm, v(-6.17, 2.19) * mm, v(-6.19, 2.1) * mm, v(-6.2, 2) * mm]});
            skFitSpline(sketch, "E311", {"points": [v(-6.2, 2) * mm, v(-6.2, 1.89) * mm, v(-6.2, 1.77) * mm, v(-6.18, 1.64) * mm]});
            skLineSegment(sketch, "E312", {"start": v(-4.9, 1.72) * mm, "end": v(-4.54, 2.55) * mm});
            skLineSegment(sketch, "E313", {"start": v(-4.54, 2.55) * mm, "end": v(-4.19, 2.4) * mm});
            skLineSegment(sketch, "E314", {"start": v(-4.19, 2.4) * mm, "end": v(-4.78, 1.03) * mm});
            skLineSegment(sketch, "E315", {"start": v(-4.78, 1.03) * mm, "end": v(-5.14, 1.18) * mm});
            skLineSegment(sketch, "E316", {"start": v(-5.14, 1.18) * mm, "end": v(-5.45, 2.14) * mm});
            skFitSpline(sketch, "E317", {"points": [v(-6.6, 1.82) * mm, v(-6.58, 1.95) * mm, v(-6.56, 2.07) * mm, v(-6.53, 2.18) * mm]});
            skFitSpline(sketch, "E318", {"points": [v(-6.53, 2.18) * mm, v(-6.5, 2.3) * mm, v(-6.47, 2.4) * mm, v(-6.42, 2.5) * mm]});
            skFitSpline(sketch, "E319", {"points": [v(-6.42, 2.5) * mm, v(-6.33, 2.74) * mm, v(-6.2, 2.89) * mm, v(-6.05, 2.97) * mm]});
            skFitSpline(sketch, "E320", {"points": [v(-6.05, 2.97) * mm, v(-5.9, 3.05) * mm, v(-5.73, 3.05) * mm, v(-5.55, 2.98) * mm]});
            skFitSpline(sketch, "E321", {"points": [v(-5.55, 2.98) * mm, v(-5.44, 2.93) * mm, v(-5.36, 2.86) * mm, v(-5.3, 2.77) * mm]});
            skFitSpline(sketch, "E322", {"points": [v(-5.3, 2.77) * mm, v(-5.23, 2.68) * mm, v(-5.16, 2.52) * mm, v(-5.08, 2.28) * mm]});
            skLineSegment(sketch, "E323", {"start": v(-6.18, 1.64) * mm, "end": v(-6.6, 1.82) * mm});
            skLineSegment(sketch, "E324", {"start": v(-6.6, 1.82) * mm, "end": v(-6.18, 1.64) * mm});
            skFitSpline(sketch, "E325", {"points": [v(-3.2, 4.76) * mm, v(-3.36, 4.97) * mm, v(-3.49, 5.1) * mm, v(-3.59, 5.16) * mm]});
            skFitSpline(sketch, "E326", {"points": [v(-3.59, 5.16) * mm, v(-3.69, 5.21) * mm, v(-3.78, 5.2) * mm, v(-3.88, 5.14) * mm]});
            skFitSpline(sketch, "E327", {"points": [v(-3.88, 5.14) * mm, v(-3.97, 5.08) * mm, v(-4, 4.98) * mm, v(-3.98, 4.87) * mm]});
            skFitSpline(sketch, "E328", {"points": [v(-3.98, 4.87) * mm, v(-3.96, 4.76) * mm, v(-3.87, 4.6) * mm, v(-3.72, 4.39) * mm]});
            skFitSpline(sketch, "E329", {"points": [v(-3.72, 4.39) * mm, v(-3.57, 4.18) * mm, v(-3.44, 4.04) * mm, v(-3.34, 3.99) * mm]});
            skFitSpline(sketch, "E330", {"points": [v(-3.34, 3.99) * mm, v(-3.24, 3.93) * mm, v(-3.14, 3.93) * mm, v(-3.05, 4) * mm]});
            skFitSpline(sketch, "E331", {"points": [v(-3.05, 4) * mm, v(-2.96, 4.07) * mm, v(-2.92, 4.16) * mm, v(-2.94, 4.27) * mm]});
            skFitSpline(sketch, "E332", {"points": [v(-2.94, 4.27) * mm, v(-2.97, 4.39) * mm, v(-3.06, 4.55) * mm, v(-3.2, 4.76) * mm]});
            skLineSegment(sketch, "E333", {"start": v(-5.08, 2.28) * mm, "end": v(-4.9, 1.72) * mm});
            skLineSegment(sketch, "E334", {"start": v(-4.9, 1.72) * mm, "end": v(-5.08, 2.28) * mm});
            skFitSpline(sketch, "E335", {"points": [v(-2.78, 5.07) * mm, v(-2.58, 4.8) * mm, v(-2.48, 4.54) * mm, v(-2.5, 4.3) * mm]});
            skFitSpline(sketch, "E336", {"points": [v(-2.5, 4.3) * mm, v(-2.5, 4.07) * mm, v(-2.62, 3.87) * mm, v(-2.83, 3.7) * mm]});
            skFitSpline(sketch, "E337", {"points": [v(-2.83, 3.7) * mm, v(-3.05, 3.55) * mm, v(-3.28, 3.5) * mm, v(-3.5, 3.56) * mm]});
            skFitSpline(sketch, "E338", {"points": [v(-3.5, 3.56) * mm, v(-3.73, 3.63) * mm, v(-3.95, 3.8) * mm, v(-4.15, 4.07) * mm]});
            skFitSpline(sketch, "E339", {"points": [v(-4.15, 4.07) * mm, v(-4.35, 4.35) * mm, v(-4.44, 4.6) * mm, v(-4.43, 4.84) * mm]});
            skFitSpline(sketch, "E340", {"points": [v(-4.43, 4.84) * mm, v(-4.42, 5.08) * mm, v(-4.3, 5.28) * mm, v(-4.09, 5.44) * mm]});
            skFitSpline(sketch, "E341", {"points": [v(-4.09, 5.44) * mm, v(-3.87, 5.6) * mm, v(-3.65, 5.64) * mm, v(-3.42, 5.58) * mm]});
            skFitSpline(sketch, "E342", {"points": [v(-3.42, 5.58) * mm, v(-3.2, 5.52) * mm, v(-2.98, 5.35) * mm, v(-2.78, 5.07) * mm]});
            skLineSegment(sketch, "E343", {"start": v(-1.12, 4.96) * mm, "end": v(-0.65, 5) * mm});
            skLineSegment(sketch, "E344", {"start": v(-0.65, 5) * mm, "end": v(-0.78, 6.33) * mm});
            skLineSegment(sketch, "E345", {"start": v(-0.78, 6.33) * mm, "end": v(-1.25, 6.18) * mm});
            skLineSegment(sketch, "E346", {"start": v(-1.25, 6.18) * mm, "end": v(-1.29, 6.54) * mm});
            skLineSegment(sketch, "E347", {"start": v(-1.29, 6.54) * mm, "end": v(-0.82, 6.69) * mm});
            skLineSegment(sketch, "E348", {"start": v(-0.82, 6.69) * mm, "end": v(-0.32, 6.74) * mm});
            skLineSegment(sketch, "E349", {"start": v(-0.32, 6.74) * mm, "end": v(-0.16, 5.05) * mm});
            skLineSegment(sketch, "E350", {"start": v(-0.16, 5.05) * mm, "end": v(0.31, 5.1) * mm});
            skLineSegment(sketch, "E351", {"start": v(0.31, 5.1) * mm, "end": v(0.35, 4.73) * mm});
            skLineSegment(sketch, "E352", {"start": v(0.35, 4.73) * mm, "end": v(-1.09, 4.6) * mm});
            skLineSegment(sketch, "E353", {"start": v(-1.09, 4.6) * mm, "end": v(-1.12, 4.96) * mm});
            skLineSegment(sketch, "E354", {"start": v(2.26, 6.42) * mm, "end": v(3.67, 5.77) * mm});
            skLineSegment(sketch, "E355", {"start": v(3.67, 5.77) * mm, "end": v(3.54, 5.5) * mm});
            skLineSegment(sketch, "E356", {"start": v(3.54, 5.5) * mm, "end": v(2.07, 4.24) * mm});
            skLineSegment(sketch, "E357", {"start": v(2.07, 4.24) * mm, "end": v(1.6, 4.46) * mm});
            skLineSegment(sketch, "E358", {"start": v(1.6, 4.46) * mm, "end": v(3, 5.65) * mm});
            skLineSegment(sketch, "E359", {"start": v(3, 5.65) * mm, "end": v(2.1, 6.07) * mm});
            skLineSegment(sketch, "E360", {"start": v(2.1, 6.07) * mm, "end": v(2.26, 6.42) * mm});
            skLineSegment(sketch, "E361", {"start": v(0.5, 11.02) * mm, "end": v(1.08, 11.05) * mm});
            skLineSegment(sketch, "E362", {"start": v(2.62, 11.45) * mm, "end": v(2.66, 12.72) * mm});
            skLineSegment(sketch, "E363", {"start": v(6.2, 8.12) * mm, "end": v(7.57, 6.97) * mm});
            skLineSegment(sketch, "E364", {"start": v(6.96, -9.71) * mm, "end": v(8.9, -11.76) * mm});
            skLineSegment(sketch, "E365", {"start": v(4, -7.35) * mm, "end": v(6.12, -10.4) * mm});
            skLineSegment(sketch, "E366", {"start": v(2.12, -13.45) * mm, "end": v(3.75, -13.1) * mm});
            skLineSegment(sketch, "E367", {"start": v(-8.06, -8.62) * mm, "end": v(-6.28, -9.99) * mm});
            skLineSegment(sketch, "E368", {"start": v(-8.06, -8.62) * mm, "end": v(-5.21, -5.46) * mm});
            skSolve(sketch);
        }
        {
            var Q0;
            Q0=makeQuery(id+"F2.imprint","IMPRINT",FACE,{"disambiguationData":[TD([[makeQuery(id+"F2.imprint","IMPRINT",EDGE,{"derivedFrom":sQuery(id+"F2.wireOp",EDGE,"E74")}),-1.0]])]});
            var Q1;
            Q1=makeQuery(id+"F2.imprint","IMPRINT",FACE,{"disambiguationData":[TD([[makeQuery(id+"F2.imprint","IMPRINT",EDGE,{"derivedFrom":sQuery(id+"F2.wireOp",EDGE,"E88")}),-1.0]])]});
            var Q2;
            Q2=makeQuery(id+"F2.imprint","IMPRINT",FACE,{"disambiguationData":[TD([[makeQuery(id+"F2.imprint","IMPRINT",EDGE,{"derivedFrom":sQuery(id+"F2.wireOp",EDGE,"E100")}),-1.0]])]});
            var Q3;
            Q3=makeQuery(id+"F2.imprint","IMPRINT",FACE,{"disambiguationData":[TD([[makeQuery(id+"F2.imprint","IMPRINT",EDGE,{"derivedFrom":sQuery(id+"F2.wireOp",EDGE,"E113")}),-1.0]])]});
            var Q4;
            Q4=makeQuery(id+"F2.imprint","IMPRINT",FACE,{"disambiguationData":[TD([[makeQuery(id+"F2.imprint","IMPRINT",EDGE,{"derivedFrom":sQuery(id+"F2.wireOp",EDGE,"E129")}),-1.0]])]});
            var Q5;
            Q5=makeQuery(id+"F2.imprint","IMPRINT",FACE,{"disambiguationData":[TD([[makeQuery(id+"F2.imprint","IMPRINT",EDGE,{"derivedFrom":sQuery(id+"F2.wireOp",EDGE,"E134")}),-1.0]])]});
            var Q6;
            Q6=makeQuery(id+"F2.imprint","IMPRINT",FACE,{"disambiguationData":[TD([[makeQuery(id+"F2.imprint","IMPRINT",EDGE,{"derivedFrom":sQuery(id+"F2.wireOp",EDGE,"E145")}),-1.0]])]});
            var Q7;
            Q7=makeQuery(id+"F2.imprint","IMPRINT",FACE,{"disambiguationData":[TD([[makeQuery(id+"F2.imprint","IMPRINT",EDGE,{"derivedFrom":sQuery(id+"F2.wireOp",EDGE,"E153")}),-1.0]])]});
            var Q8;
            Q8=makeQuery(id+"F2.imprint","IMPRINT",FACE,{"disambiguationData":[TD([[makeQuery(id+"F2.imprint","IMPRINT",EDGE,{"derivedFrom":sQuery(id+"F2.wireOp",EDGE,"E157")}),-1.0]])]});
            var Q9;
            Q9=makeQuery(id+"F2.imprint","IMPRINT",FACE,{"disambiguationData":[TD([[makeQuery(id+"F2.imprint","IMPRINT",EDGE,{"derivedFrom":sQuery(id+"F2.wireOp",EDGE,"E174")}),1.0]])]});
            var Q10;
            Q10=makeQuery(id+"F2.imprint","IMPRINT",FACE,{"disambiguationData":[TD([[makeQuery(id+"F2.imprint","IMPRINT",EDGE,{"derivedFrom":sQuery(id+"F2.wireOp",EDGE,"E187")}),1.0]])]});
            var Q11;
            Q11=makeQuery(id+"F2.imprint","IMPRINT",FACE,{"disambiguationData":[TD([[makeQuery(id+"F2.imprint","IMPRINT",EDGE,{"derivedFrom":sQuery(id+"F2.wireOp",EDGE,"E198")}),-1.0]])]});
            var Q12;
            Q12=makeQuery(id+"F2.imprint","IMPRINT",FACE,{"disambiguationData":[TD([[makeQuery(id+"F2.imprint","IMPRINT",EDGE,{"derivedFrom":sQuery(id+"F2.wireOp",EDGE,"E194")}),-1.0]])]});
            var Q13;
            Q13=makeQuery(id+"F2.imprint","IMPRINT",FACE,{"disambiguationData":[TD([[makeQuery(id+"F2.imprint","IMPRINT",EDGE,{"derivedFrom":sQuery(id+"F2.wireOp",EDGE,"E2")}),-1.0]])]});
            var Q14;
            Q14=makeQuery(id+"F2.imprint","IMPRINT",FACE,{"disambiguationData":[TD([[makeQuery(id+"F2.imprint","IMPRINT",EDGE,{"derivedFrom":sQuery(id+"F2.wireOp",EDGE,"E10")}),-1.0]])]});
            var Q15;
            Q15=makeQuery(id+"F2.imprint","IMPRINT",FACE,{"disambiguationData":[TD([[makeQuery(id+"F2.imprint","IMPRINT",EDGE,{"derivedFrom":sQuery(id+"F2.wireOp",EDGE,"E21")}),-1.0]])]});
            var Q16;
            Q16=makeQuery(id+"F2.imprint","IMPRINT",FACE,{"disambiguationData":[TD([[makeQuery(id+"F2.imprint","IMPRINT",EDGE,{"derivedFrom":sQuery(id+"F2.wireOp",EDGE,"E38")}),-1.0]])]});
            var Q17;
            Q17=makeQuery(id+"F2.imprint","IMPRINT",FACE,{"disambiguationData":[TD([[makeQuery(id+"F2.imprint","IMPRINT",EDGE,{"derivedFrom":sQuery(id+"F2.wireOp",EDGE,"E46")}),-1.0]])]});
            var Q18;
            Q18=makeQuery(id+"F2.imprint","IMPRINT",FACE,{"disambiguationData":[TD([[makeQuery(id+"F2.imprint","IMPRINT",EDGE,{"derivedFrom":sQuery(id+"F2.wireOp",EDGE,"E56")}),-1.0]])]});
            var Q19;
            Q19=makeQuery(id+"F2.imprint","IMPRINT",FACE,{"disambiguationData":[TD([[makeQuery(id+"F2.imprint","IMPRINT",EDGE,{"derivedFrom":sQuery(id+"F2.wireOp",EDGE,"E75")}),-1.0]])]});
            extrude(context, id + "F3", {"entities" : qUnion([Q0, Q1, Q2, Q3, Q4, Q5, Q6, Q7, Q8, Q9, Q10, Q11, Q12, Q13, Q14, Q15, Q16, Q17, Q18, Q19]), "operationType" : NewBodyOperationType.ADD, "depth" : 2 * mm, "offsetDistance" : 25 * mm});
        }
        {
            var Q0;
            Q0=makeQuery(id+"F2.imprint","IMPRINT",FACE,{"disambiguationData":[TD([[makeQuery(id+"F2.imprint","IMPRINT",EDGE,{"derivedFrom":sQuery(id+"F2.wireOp",EDGE,"E306")}),-1.0]])]});
            var Q1;
            Q1=makeQuery(id+"F2.imprint","IMPRINT",FACE,{"disambiguationData":[TD([[makeQuery(id+"F2.imprint","IMPRINT",EDGE,{"derivedFrom":sQuery(id+"F2.wireOp",EDGE,"E325")}),-1.0]])]});
            var Q2;
            Q2=makeQuery(id+"F2.imprint","IMPRINT",FACE,{"disambiguationData":[TD([[makeQuery(id+"F2.imprint","IMPRINT",EDGE,{"derivedFrom":sQuery(id+"F2.wireOp",EDGE,"E343")}),-1.0]])]});
            var Q3;
            Q3=makeQuery(id+"F2.imprint","IMPRINT",FACE,{"disambiguationData":[TD([[makeQuery(id+"F2.imprint","IMPRINT",EDGE,{"derivedFrom":sQuery(id+"F2.wireOp",EDGE,"E354")}),-1.0]])]});
            var Q4;
            Q4=makeQuery(id+"F2.imprint","IMPRINT",FACE,{"disambiguationData":[TD([[makeQuery(id+"F2.imprint","IMPRINT",EDGE,{"derivedFrom":sQuery(id+"F2.wireOp",EDGE,"E213")}),-1.0]])]});
            var Q5;
            Q5=makeQuery(id+"F2.imprint","IMPRINT",FACE,{"disambiguationData":[TD([[makeQuery(id+"F2.imprint","IMPRINT",EDGE,{"derivedFrom":sQuery(id+"F2.wireOp",EDGE,"E254")}),-1.0]])]});
            var Q6;
            Q6=makeQuery(id+"F2.imprint","IMPRINT",FACE,{"disambiguationData":[TD([[makeQuery(id+"F2.imprint","IMPRINT",EDGE,{"derivedFrom":sQuery(id+"F2.wireOp",EDGE,"E276")}),-1.0]])]});
            var Q7;
            Q7=makeQuery(id+"F2.imprint","IMPRINT",FACE,{"disambiguationData":[TD([[makeQuery(id+"F2.imprint","IMPRINT",EDGE,{"derivedFrom":sQuery(id+"F2.wireOp",EDGE,"E292")}),-1.0]])]});
            var Q8;
            Q8=makeQuery(id+"F2.imprint","IMPRINT",FACE,{"disambiguationData":[TD([[makeQuery(id+"F2.imprint","IMPRINT",EDGE,{"derivedFrom":sQuery(id+"F2.wireOp",EDGE,"E302")}),-1.0]])]});
            var Q9;
            Q9=makeQuery(id+"F2.imprint","IMPRINT",FACE,{"disambiguationData":[TD([[makeQuery(id+"F2.imprint","IMPRINT",EDGE,{"derivedFrom":sQuery(id+"F2.wireOp",EDGE,"E297")}),-1.0]])]});
            extrude(context, id + "F4", {"entities" : qUnion([Q0, Q1, Q2, Q3, Q4, Q5, Q6, Q7, Q8, Q9]), "operationType" : NewBodyOperationType.ADD, "depth" : 1 * mm, "offsetDistance" : 25 * mm});
        }
    });
